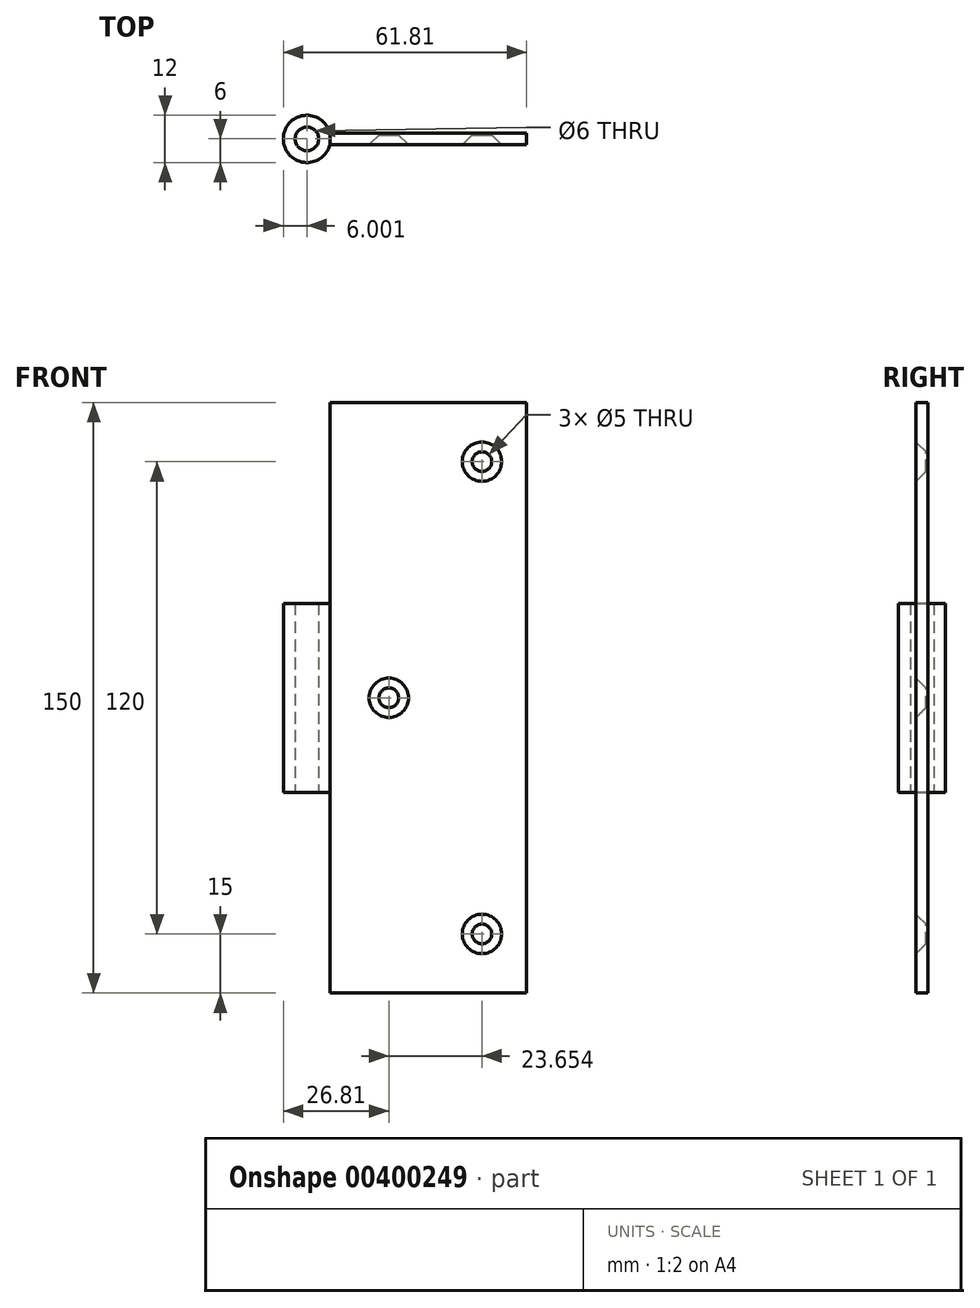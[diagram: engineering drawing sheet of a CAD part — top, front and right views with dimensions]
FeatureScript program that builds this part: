
annotation { "Feature Type Name" : "Feature", "Feature Type Description" : "" }
export const myFeature = defineFeature(function(context is Context, id is Id, definition is map)
    precondition{}
    {
        {
            var Q0;
            Q0=qCreatedBy(makeId("Top.planeOp"),FACE);
            var sketch = newSketch(context, id + "F0", { "sketchPlane" : qUnion([Q0])});
            skLineSegment(sketch, "E0.bottom", {"start": v(0, 0) * mm, "end": v(50, 0) * mm});
            skLineSegment(sketch, "E0.top", {"start": v(0, 3) * mm, "end": v(50, 3) * mm});
            skLineSegment(sketch, "E0.right", {"start": v(50, 0) * mm, "end": v(50, 3) * mm});
            skLineSegment(sketch, "E1", {"start": v(0, 3) * mm, "end": v(0, 0) * mm});
            skSolve(sketch);
        }
        {
            var Q0;
            Q0=qSketchRegion(id+"F0",true);
            var Q1;
            Q1=qSketchRegion(id+"F2",true);
            extrude(context, id + "F1", {"entities" : qUnion([Q0, Q1]), "depth" : 150 * mm});
        }
        {
            var Q0;
            Q0=qCreatedBy(makeId("Top.planeOp"),FACE);
            var sketch = newSketch(context, id + "F2", { "sketchPlane" : qUnion([Q0])});
            skPoint(sketch, "E2.0", {"position": v(0, 1.5) * mm});
            skCircle(sketch, "E3", {"center": v(-5.8, 1.5) * mm, "radius": 6 * mm});
            skCircle(sketch, "E4", {"center": v(-5.8, 1.5) * mm, "radius": 3 * mm});
            skSolve(sketch);
        }
        {
            var Q0;
            Q0=qSketchRegion(id+"F2",true);
            var Q1;
            Q1=makeQuery(id+"F1.opExtrude","CAP_FACE",FACE,{"disambiguationData":[OSD([sQuery(id+"F0.wireOp",EDGE,"E0.bottom"),sQuery(id+"F0.wireOp",EDGE,"E0.top"),sQuery(id+"F0.wireOp",EDGE,"E0.right"),sQuery(id+"F0.wireOp",EDGE,"E1")])],"isStart":false});
            extrude(context, id + "F3", {"entities" : qUnion([Q0]), "operationType" : NewBodyOperationType.ADD, "endBoundEntityFace" : qUnion([Q1]), "depth" : 99 * mm, "hasSecondDirection" : true, "secondDirectionOppositeDirection" : false, "secondDirectionDepth" : 51 * mm});
        }
        {
            var Q0;
            Q0=qCreatedBy(makeId("Front.planeOp"),FACE);
            var sketch = newSketch(context, id + "F4", { "sketchPlane" : qUnion([Q0])});
            skPoint(sketch, "E5", {"position": v(38.65, 135) * mm});
            skPoint(sketch, "E6", {"position": v(38.65, 15) * mm});
            skPoint(sketch, "E7", {"position": v(15, 75) * mm});
            skPoint(sketch, "E8.0", {"position": v(50, 75) * mm});
            skSolve(sketch);
        }
        {
            var Q0;
            Q0=sQuery(id+"F4.wireOp",VERTEX,"E5");
            var Q1;
            Q1=sQuery(id+"F4.wireOp",VERTEX,"E7");
            var Q2;
            Q2=sQuery(id+"F4.wireOp",VERTEX,"E6");
            var Q3;
            Q3=makeQuery(id+"F1.opExtrude","SWEPT_BODY",BODY,{"disambiguationData":[OSD([sQuery(id+"F0.wireOp",EDGE,"E0.bottom"),sQuery(id+"F0.wireOp",EDGE,"E0.top"),sQuery(id+"F0.wireOp",EDGE,"E0.right"),sQuery(id+"F0.wireOp",EDGE,"E1")])]});
            hole(context, id + "F5", {"style" : HoleStyle.C_SINK, "endStyle" : HoleEndStyle.THROUGH, "holeDiameter" : 5 * mm, "cSinkDiameter" : 10 * mm, "cSinkAngle" : 90 * degree, "isTappedThrough" : true, "tappedDepth" : 12 * mm, "tapClearance" : 3, "locations" : qUnion([Q0, Q1, Q2]), "scope" : qUnion([Q3])});
        }
    });
